# Revit family: Gira_536327
name_source: partatom
category: Electrical Fixtures
revit_build: Autodesk Revit 2017 (Build: 20160225_1515(x64)
units: mm (PartAtom-declared; Revit-internal decimal feet)

## family parameters
Cut with Voids When Loaded = No
Host = Face
Maintain Annotation Orientation = No
Part Type = Normal
Room Calculation Point = No
Round Connector Dimension = Use Diameter
Shared = No

## types (1)
- S3000 Bedienaufs. Memory System 55 Reinweiß m
    Anwendung = Steuern elektrischer Verbraucher
    Anzahl der Betätigungspunkte = 4
    Anzahl der Tasten = 2
    Ausführung der Oberfläche = matt
    Available = Yes
    Category = Bedienelement intelligent
    Data sheet (1) = https://katalog.gira.de
    Default Elevation = 1219 mm
    Farbe = weiß
    GTIN = 4010337027379
    Geeignet für Dimmeinsatz = No
    Geeignet für Jalousieeinsatz = Yes
    Geeignet für Schalteinsatz = No
    HAN = 536327
    Halogenfrei = Yes
    HeinzeBIM = https://bimportal.heinze.de
    Keynote = Sys55_Abdeckung_Schalten und Tasten
    Manufacturer URL = https://www.gira.de
    Mit Abdeckung = Yes
    Mit LED-Anzeige = No
    Name = S3000 Bedienaufs. Memory System 55 Reinweiß m
    Oberfläche = sonstige
    RAL-Nummer (ähnlich) = 9010
    Region = DE
    Transparent = No
    URL = http://katalog.gira.de
    Werkstoff = sonstige
    Werkstoffgüte = sonstige

## geometry (parser evidence)
native form markers: Blend x2, Sweep x9
no freeform markers — native parametric forms only
